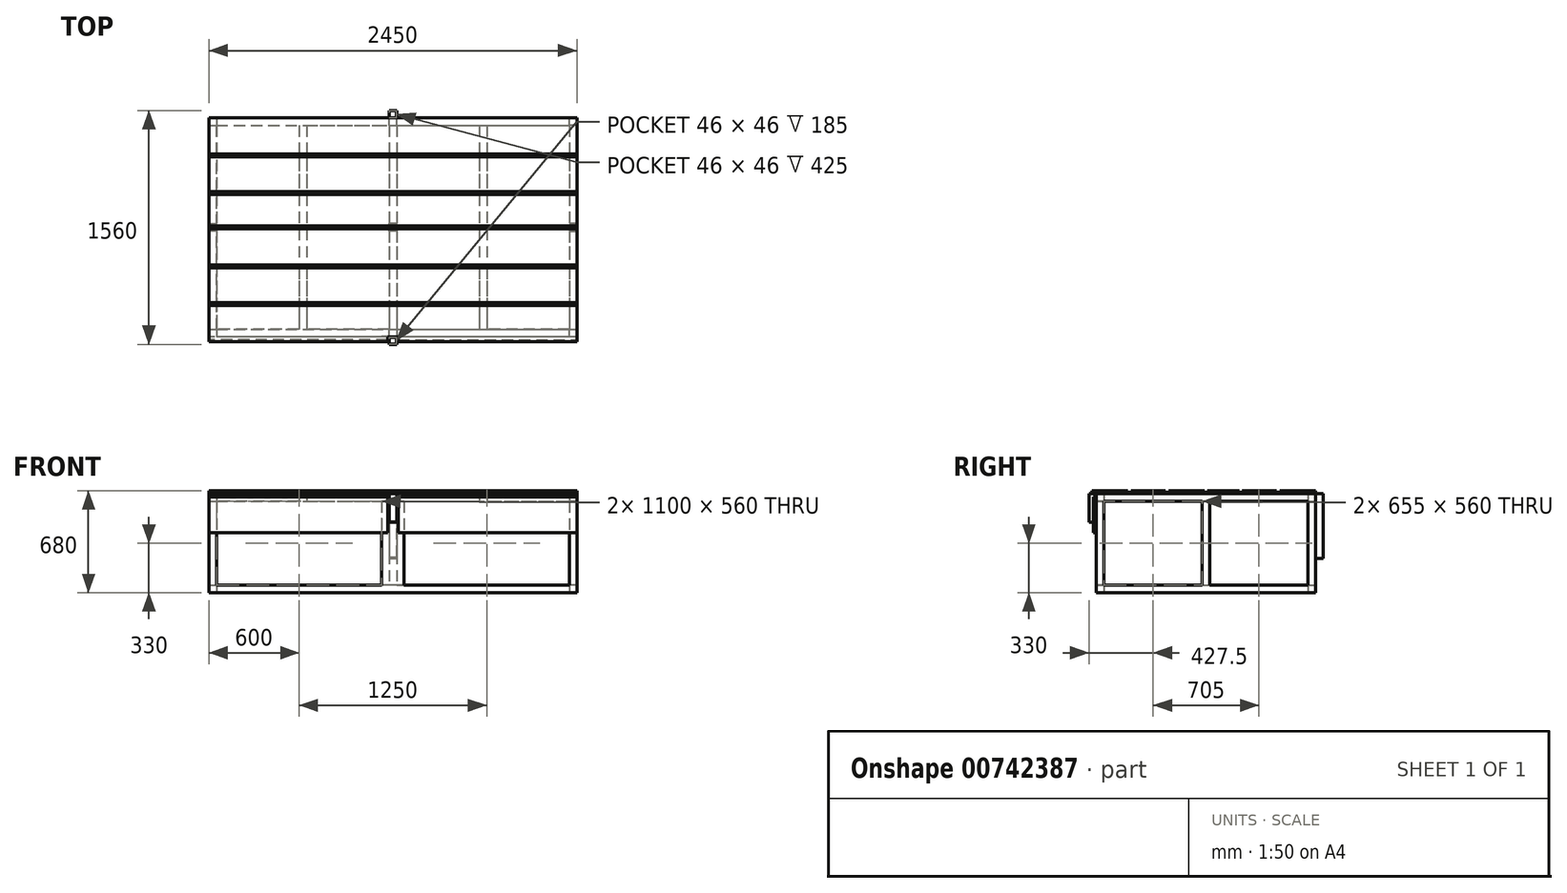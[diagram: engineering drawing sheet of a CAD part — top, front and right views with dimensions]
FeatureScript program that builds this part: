
annotation { "Feature Type Name" : "Feature", "Feature Type Description" : "" }
export const myFeature = defineFeature(function(context is Context, id is Id, definition is map)
    precondition{}
    {
        {
            var Q0;
            Q0=qCreatedBy(makeId("Top.planeOp"),FACE);
            var sketch = newSketch(context, id + "F0", { "sketchPlane" : qUnion([Q0])});
            skLineSegment(sketch, "E0.bottom", {"start": v(1225, -730) * mm, "end": v(-1225, -730) * mm});
            skLineSegment(sketch, "E0.top", {"start": v(1225, 730) * mm, "end": v(-1225, 730) * mm});
            skLineSegment(sketch, "E0.left", {"start": v(1225, -730) * mm, "end": v(1225, 730) * mm});
            skLineSegment(sketch, "E0.right", {"start": v(-1225, -730) * mm, "end": v(-1225, 730) * mm});
            skPoint(sketch, "E0.middle", {"position": v(0, 0) * mm});
            skLineSegment(sketch, "E1.bottom", {"start": v(-1175, 680) * mm, "end": v(1175, 680) * mm});
            skLineSegment(sketch, "E1.top", {"start": v(-1175, -680) * mm, "end": v(1175, -680) * mm});
            skLineSegment(sketch, "E1.left", {"start": v(-1175, 680) * mm, "end": v(-1175, -680) * mm});
            skLineSegment(sketch, "E1.right", {"start": v(1175, 680) * mm, "end": v(1175, -680) * mm});
            skLineSegment(sketch, "E2.bottom", {"start": v(25, 680) * mm, "end": v(-25, 680) * mm});
            skLineSegment(sketch, "E2.top", {"start": v(25, -680) * mm, "end": v(-25, -680) * mm});
            skLineSegment(sketch, "E2.left", {"start": v(25, 680) * mm, "end": v(25, -680) * mm});
            skLineSegment(sketch, "E2.right", {"start": v(-25, 680) * mm, "end": v(-25, -680) * mm});
            skSolve(sketch);
        }
        {
            var Q0;
            Q0=qSketchRegion(id+"F0",true);
            var Q1;
            Q1=makeQuery(id+"F0.imprint","IMPRINT",FACE,{"disambiguationData":[TD([[makeQuery(id+"F0.imprint","IMPRINT",EDGE,{"derivedFrom":sQuery(id+"F0.wireOp",EDGE,"E2.bottom")}),1.0]])]});
            extrude(context, id + "F1", {"entities" : qUnion([Q0, Q1]), "depth" : 50 * mm, "offsetDistance" : 25 * mm});
        }
        {
            var Q0;
            Q0=makeQuery(id+"F1.opExtrude","CAP_FACE",FACE,{"disambiguationData":[OSD([sQuery(id+"F0.wireOp",EDGE,"E0.bottom"),sQuery(id+"F0.wireOp",EDGE,"E0.top"),sQuery(id+"F0.wireOp",EDGE,"E0.left"),sQuery(id+"F0.wireOp",EDGE,"E0.right"),sQuery(id+"F0.wireOp",EDGE,"E1.bottom"),sQuery(id+"F0.wireOp",EDGE,"E1.top"),sQuery(id+"F0.wireOp",EDGE,"E1.left"),sQuery(id+"F0.wireOp",EDGE,"E1.right"),sQuery(id+"F0.wireOp",EDGE,"E2.left"),sQuery(id+"F0.wireOp",EDGE,"E2.right")])],"isStart":false});
            var sketch = newSketch(context, id + "F2", { "sketchPlane" : qUnion([Q0])});
            skLineSegment(sketch, "E3.bottom", {"start": v(-1225, 730) * mm, "end": v(-1175, 730) * mm});
            skLineSegment(sketch, "E3.top", {"start": v(-1225, 680) * mm, "end": v(-1175, 680) * mm});
            skLineSegment(sketch, "E3.left", {"start": v(-1225, 730) * mm, "end": v(-1225, 680) * mm});
            skLineSegment(sketch, "E3.right", {"start": v(-1175, 730) * mm, "end": v(-1175, 680) * mm});
            skLineSegment(sketch, "E4", {"start": v(-25, 680) * mm, "end": v(-25, 730) * mm});
            skLineSegment(sketch, "E5", {"start": v(25, 680) * mm, "end": v(25, 730) * mm});
            skLineSegment(sketch, "E6", {"start": v(25, 730) * mm, "end": v(-25, 730) * mm});
            skLineSegment(sketch, "E7", {"start": v(-25, 680) * mm, "end": v(25, 680) * mm});
            skLineSegment(sketch, "E8", {"start": v(1175, 680) * mm, "end": v(1175, 730) * mm});
            skLineSegment(sketch, "E9", {"start": v(1175, 730) * mm, "end": v(1225, 730) * mm});
            skLineSegment(sketch, "E10", {"start": v(1225, 730) * mm, "end": v(1225, 680) * mm});
            skLineSegment(sketch, "E11", {"start": v(1225, 680) * mm, "end": v(1175, 680) * mm});
            skLineSegment(sketch, "E12", {"start": v(1175, -680) * mm, "end": v(1225, -680) * mm});
            skLineSegment(sketch, "E13", {"start": v(1225, -680) * mm, "end": v(1225, -730) * mm});
            skLineSegment(sketch, "E14", {"start": v(1225, -730) * mm, "end": v(1175, -730) * mm});
            skLineSegment(sketch, "E15", {"start": v(1175, -730) * mm, "end": v(1175, -680) * mm});
            skLineSegment(sketch, "E16", {"start": v(-25, -680) * mm, "end": v(25, -680) * mm});
            skLineSegment(sketch, "E17", {"start": v(25, -680) * mm, "end": v(25, -730) * mm});
            skLineSegment(sketch, "E18", {"start": v(25, -730) * mm, "end": v(-25, -730) * mm});
            skLineSegment(sketch, "E19", {"start": v(-25, -730) * mm, "end": v(-25, -680) * mm});
            skLineSegment(sketch, "E20", {"start": v(-1175, -680) * mm, "end": v(-1175, -730) * mm});
            skLineSegment(sketch, "E21", {"start": v(-1175, -730) * mm, "end": v(-1225, -730) * mm});
            skLineSegment(sketch, "E22", {"start": v(-1225, -730) * mm, "end": v(-1225, -680) * mm});
            skLineSegment(sketch, "E23", {"start": v(-1225, -680) * mm, "end": v(-1175, -680) * mm});
            skLineSegment(sketch, "E24.bottom", {"start": v(25, -25) * mm, "end": v(-25, -25) * mm});
            skLineSegment(sketch, "E24.top", {"start": v(25, 25) * mm, "end": v(-25, 25) * mm});
            skLineSegment(sketch, "E24.left", {"start": v(25, -25) * mm, "end": v(25, 25) * mm});
            skLineSegment(sketch, "E24.right", {"start": v(-25, -25) * mm, "end": v(-25, 25) * mm});
            skPoint(sketch, "E24.middle", {"position": v(0, 0) * mm});
            skLineSegment(sketch, "E25", {"start": v(0, 0) * mm, "end": v(-1225, 0) * mm});
            skLineSegment(sketch, "E26", {"start": v(-1225, 25) * mm, "end": v(-1175, 25) * mm});
            skLineSegment(sketch, "E27", {"start": v(-1175, 25) * mm, "end": v(-1175, -25) * mm});
            skLineSegment(sketch, "E28", {"start": v(-1175, -25) * mm, "end": v(-1225, -25) * mm});
            skLineSegment(sketch, "E29", {"start": v(-1225, 25) * mm, "end": v(-1225, -25) * mm});
            skLineSegment(sketch, "E30.MirrorCS", {"start": v(1225, 25) * mm, "end": v(1225, -25) * mm});
            skLineSegment(sketch, "E31.MirrorCS", {"start": v(1175, -25) * mm, "end": v(1225, -25) * mm});
            skLineSegment(sketch, "E32.MirrorCS", {"start": v(1225, 25) * mm, "end": v(1175, 25) * mm});
            skLineSegment(sketch, "E33.MirrorCS", {"start": v(1175, 25) * mm, "end": v(1175, -25) * mm});
            skSolve(sketch);
        }
        {
            var Q0;
            Q0=qSketchRegion(id+"F2",true);
            extrude(context, id + "F3", {"entities" : qUnion([Q0]), "operationType" : NewBodyOperationType.ADD, "depth" : 560 * mm, "offsetDistance" : 25 * mm});
        }
        {
            var Q0;
            Q0=makeQuery(id+"F3.opExtrude","CAP_FACE",FACE,{"disambiguationData":[OSD([sQuery(id+"F2.wireOp",EDGE,"E26"),sQuery(id+"F2.wireOp",EDGE,"E27"),sQuery(id+"F2.wireOp",EDGE,"E28"),sQuery(id+"F2.wireOp",EDGE,"E29")])],"isStart":false});
            var sketch = newSketch(context, id + "F4", { "sketchPlane" : qUnion([Q0])});
            skLineSegment(sketch, "E34", {"start": v(-1225, 25) * mm, "end": v(-1225, 730) * mm});
            skLineSegment(sketch, "E35", {"start": v(-1225, 730) * mm, "end": v(-1175, 730) * mm});
            skLineSegment(sketch, "E36", {"start": v(-1175, 730) * mm, "end": v(1225, 730) * mm});
            skLineSegment(sketch, "E37", {"start": v(1225, 730) * mm, "end": v(1225, -730) * mm});
            skLineSegment(sketch, "E38", {"start": v(1225, -730) * mm, "end": v(-1225, -730) * mm});
            skLineSegment(sketch, "E39", {"start": v(-1225, -730) * mm, "end": v(-1225, 25) * mm});
            skLineSegment(sketch, "E40", {"start": v(-1175, 730) * mm, "end": v(-1175, 680) * mm});
            skLineSegment(sketch, "E41", {"start": v(-1175, 680) * mm, "end": v(-25, 680) * mm});
            skLineSegment(sketch, "E42", {"start": v(-1175, 680) * mm, "end": v(-600, 680) * mm});
            skLineSegment(sketch, "E43", {"start": v(-600, 680) * mm, "end": v(-575, 680) * mm});
            skLineSegment(sketch, "E44", {"start": v(-600, 680) * mm, "end": v(-625, 680) * mm});
            skLineSegment(sketch, "E45", {"start": v(-625, 680) * mm, "end": v(-625, -680) * mm});
            skLineSegment(sketch, "E46.MirrorCS", {"start": v(-575, 680) * mm, "end": v(-575, -680) * mm});
            skLineSegment(sketch, "E47", {"start": v(-25, 680) * mm, "end": v(25, 680) * mm});
            skLineSegment(sketch, "E48", {"start": v(25, 680) * mm, "end": v(1175, 680) * mm});
            skLineSegment(sketch, "E49", {"start": v(25, 680) * mm, "end": v(600, 680) * mm});
            skLineSegment(sketch, "E50", {"start": v(600, 680) * mm, "end": v(575, 680) * mm});
            skLineSegment(sketch, "E51", {"start": v(575, 680) * mm, "end": v(575, -680) * mm});
            skLineSegment(sketch, "E52.MirrorCS", {"start": v(625, 680) * mm, "end": v(625, -680) * mm});
            skLineSegment(sketch, "E53", {"start": v(-25, 680) * mm, "end": v(-25, -680) * mm});
            skLineSegment(sketch, "E54", {"start": v(-25, -680) * mm, "end": v(-575, -680) * mm});
            skLineSegment(sketch, "E55", {"start": v(-625, -680) * mm, "end": v(-1175, -680) * mm});
            skLineSegment(sketch, "E56", {"start": v(-1175, -680) * mm, "end": v(-1175, 680) * mm});
            skLineSegment(sketch, "E57", {"start": v(1175, 680) * mm, "end": v(1175, -680) * mm});
            skLineSegment(sketch, "E58", {"start": v(1175, -680) * mm, "end": v(625, -680) * mm});
            skLineSegment(sketch, "E59", {"start": v(25, 680) * mm, "end": v(25, -680) * mm});
            skLineSegment(sketch, "E60", {"start": v(25, -680) * mm, "end": v(575, -680) * mm});
            skSolve(sketch);
        }
        {
            var Q0;
            Q0=qSketchRegion(id+"F4",true);
            extrude(context, id + "F5", {"entities" : qUnion([Q0]), "operationType" : NewBodyOperationType.ADD, "depth" : 50 * mm, "offsetDistance" : 25 * mm});
        }
        {
            var Q0;
            {var subQ5=sQuery(id+"F0.wireOp",EDGE,"E1.left");var subQ6=sQuery(id+"F0.wireOp",EDGE,"E1.top");var subQ8=makeQuery(id+"F1.opExtrude","CAP_EDGE",EDGE,{"disambiguationData":[OSD([subQ6]),TDD([makeQuery(id+"F0.imprint","IMPRINT",EDGE,{"disambiguationData":[TD([[makeQuery(id+"F0.imprint","INTERSECT",VERTEX,{"derivedFrom":[subQ6,subQ5]}),-1.0]])],"derivedFrom":subQ6})])],"isStart":false});Q0=makeQuery(id+"F2.imprint","IMPRINT",FACE,{"disambiguationData":[TD([[makeQuery(id+"F2.imprint","IMPRINT",EDGE,{"derivedFrom":subQ8}),1.0]])]});}
            cPlane(context, id + "F6", {"entities" : qUnion([Q0]), "cplaneType" : CPlaneType.OFFSET, "offset" : 420 * mm, "width" : 150 * mm, "height" : 150 * mm});
        }
        {
            var Q0;
            Q0=qCreatedBy(id+"F6.planeOp",FACE);
            var sketch = newSketch(context, id + "F7", { "sketchPlane" : qUnion([Q0])});
            skLineSegment(sketch, "E61.bottom", {"start": v(-25, -730) * mm, "end": v(25, -730) * mm});
            skLineSegment(sketch, "E61.top", {"start": v(-25, -780) * mm, "end": v(25, -780) * mm});
            skLineSegment(sketch, "E61.left", {"start": v(-25, -730) * mm, "end": v(-25, -780) * mm});
            skLineSegment(sketch, "E61.right", {"start": v(25, -730) * mm, "end": v(25, -780) * mm});
            skSolve(sketch);
        }
        {
            var Q0;
            Q0 = qSketchRegion(id + "F7", true);
            extrude(context, id + "F8", {"entities" : qUnion([Q0]), "operationType" : NewBodyOperationType.ADD, "depth" : 5 * mm, "offsetDistance" : 25 * mm});
        }
        {
            var Q0;
            Q0=makeQuery(id+"F8.opExtrude","CAP_FACE",FACE,{"disambiguationData":[OSD([sQuery(id+"F7.wireOp",EDGE,"E61.bottom"),sQuery(id+"F7.wireOp",EDGE,"E61.top"),sQuery(id+"F7.wireOp",EDGE,"E61.left"),sQuery(id+"F7.wireOp",EDGE,"E61.right")])],"isStart":false});
            var sketch = newSketch(context, id + "F9", { "sketchPlane" : qUnion([Q0])});
            skLineSegment(sketch, "E62.bottom", {"start": v(-25, -730) * mm, "end": v(25, -730) * mm});
            skLineSegment(sketch, "E62.top", {"start": v(-25, -780) * mm, "end": v(25, -780) * mm});
            skLineSegment(sketch, "E62.left", {"start": v(-25, -730) * mm, "end": v(-25, -780) * mm});
            skLineSegment(sketch, "E62.right", {"start": v(25, -730) * mm, "end": v(25, -780) * mm});
            skLineSegment(sketch, "E63.bottom", {"start": v(25, -780) * mm, "end": v(23, -780) * mm});
            skLineSegment(sketch, "E63.top", {"start": v(25, -778) * mm, "end": v(23, -778) * mm});
            skLineSegment(sketch, "E63.left", {"start": v(25, -780) * mm, "end": v(25, -778) * mm});
            skLineSegment(sketch, "E63.right", {"start": v(23, -780) * mm, "end": v(23, -778) * mm});
            skLineSegment(sketch, "E64.bottom", {"start": v(23, -778) * mm, "end": v(-23, -778) * mm});
            skLineSegment(sketch, "E64.top", {"start": v(23, -732) * mm, "end": v(-23, -732) * mm});
            skLineSegment(sketch, "E64.left", {"start": v(23, -778) * mm, "end": v(23, -732) * mm});
            skLineSegment(sketch, "E64.right", {"start": v(-23, -778) * mm, "end": v(-23, -732) * mm});
            skSolve(sketch);
        }
        {
            var Q0;
            Q0 = qSketchRegion(id + "F9", true);
            var Q1;
            {var subQ0=sQuery(id+"F4.wireOp",EDGE,"E60");var subQ1=sQuery(id+"F4.wireOp",EDGE,"E59");var subQ2=sQuery(id+"F4.wireOp",EDGE,"E58");var subQ3=sQuery(id+"F4.wireOp",EDGE,"E57");var subQ4=sQuery(id+"F4.wireOp",EDGE,"E56");var subQ5=sQuery(id+"F4.wireOp",EDGE,"E55");var subQ6=sQuery(id+"F4.wireOp",EDGE,"E54");var subQ7=sQuery(id+"F4.wireOp",EDGE,"E53");var subQ8=sQuery(id+"F4.wireOp",EDGE,"E52.MirrorCS");var subQ9=sQuery(id+"F4.wireOp",EDGE,"E51");var subQ10=sQuery(id+"F4.wireOp",EDGE,"E49");var subQ11=sQuery(id+"F4.wireOp",EDGE,"E48");var subQ12=sQuery(id+"F4.wireOp",EDGE,"E46.MirrorCS");var subQ13=sQuery(id+"F4.wireOp",EDGE,"E45");var subQ14=sQuery(id+"F4.wireOp",EDGE,"E42");var subQ15=sQuery(id+"F4.wireOp",EDGE,"E41");var subQ16=sQuery(id+"F4.wireOp",EDGE,"E39");var subQ17=sQuery(id+"F4.wireOp",EDGE,"E38");var subQ18=sQuery(id+"F4.wireOp",EDGE,"E37");var subQ19=sQuery(id+"F4.wireOp",EDGE,"E36");var subQ20=sQuery(id+"F4.wireOp",EDGE,"E35");var subQ21=sQuery(id+"F4.wireOp",EDGE,"E34");Q1=makeQuery(id+"FP4IzDu3Lu8PIDH_1.boolean.opBoolean","MERGE",FACE,{"derivedFrom":[makeQuery(id+"F5.opExtrude","CAP_FACE",FACE,{"disambiguationData":[OSD([subQ21,subQ20,subQ19,subQ18,subQ17,subQ16,subQ15,subQ14,subQ13,subQ12,subQ11,subQ10,subQ9,subQ8,subQ7,subQ6,subQ5,subQ4,subQ3,subQ2,subQ1,subQ0])],"isStart":false}),makeQuery(id+"FP4IzDu3Lu8PIDH_1.opExtrude","CAP_FACE",FACE,{"disambiguationData":[OSD([subQ21,subQ20,subQ19,subQ18,subQ17,subQ16,subQ15,subQ14,subQ13,subQ12,subQ11,subQ10,subQ9,subQ8,subQ7,subQ6,subQ5,subQ4,subQ3,subQ2,subQ1,subQ0])],"isStart":false})]});}
            extrude(context, id + "F10", {"entities" : qUnion([Q0]), "operationType" : NewBodyOperationType.ADD, "endBound" : BoundingType.UP_TO_SURFACE, "depth" : 25 * mm, "endBoundEntityFace" : qUnion([Q1]), "offsetDistance" : 25 * mm});
        }
        {
            var Q0;
            {var subQ5=sQuery(id+"F0.wireOp",EDGE,"E1.left");var subQ6=sQuery(id+"F0.wireOp",EDGE,"E1.top");var subQ8=makeQuery(id+"F1.opExtrude","CAP_EDGE",EDGE,{"disambiguationData":[OSD([subQ6]),TDD([makeQuery(id+"F0.imprint","IMPRINT",EDGE,{"disambiguationData":[TD([[makeQuery(id+"F0.imprint","INTERSECT",VERTEX,{"derivedFrom":[subQ6,subQ5]}),-1.0]])],"derivedFrom":subQ6})])],"isStart":false});Q0=makeQuery(id+"F2.imprint","IMPRINT",FACE,{"disambiguationData":[TD([[makeQuery(id+"F2.imprint","IMPRINT",EDGE,{"derivedFrom":subQ8}),1.0]])]});}
            cPlane(context, id + "F11", {"entities" : qUnion([Q0]), "cplaneType" : CPlaneType.OFFSET, "offset" : 180 * mm, "width" : 150 * mm, "height" : 150 * mm});
        }
        {
            var Q0;
            Q0=qCreatedBy(id+"F11.planeOp",FACE);
            var sketch = newSketch(context, id + "F12", { "sketchPlane" : qUnion([Q0])});
            skLineSegment(sketch, "E65.bottom", {"start": v(-25, 730) * mm, "end": v(25, 730) * mm});
            skLineSegment(sketch, "E65.top", {"start": v(-25, 780) * mm, "end": v(25, 780) * mm});
            skLineSegment(sketch, "E65.left", {"start": v(-25, 730) * mm, "end": v(-25, 780) * mm});
            skLineSegment(sketch, "E65.right", {"start": v(25, 730) * mm, "end": v(25, 780) * mm});
            skSolve(sketch);
        }
        {
            var Q0;
            Q0=makeQuery(id+"F12.imprint","IMPRINT",FACE,{"disambiguationData":[TD([[makeQuery(id+"F12.imprint","IMPRINT",EDGE,{"derivedFrom":sQuery(id+"F12.wireOp",EDGE,"E65.bottom")}),1.0]])]});
            extrude(context, id + "F13", {"entities" : qUnion([Q0]), "operationType" : NewBodyOperationType.ADD, "depth" : 5 * mm, "offsetDistance" : 25 * mm});
        }
        {
            var Q0;
            Q0=makeQuery(id+"F3.opExtrude","SWEPT_FACE",FACE,{"disambiguationData":[OSD([sQuery(id+"F2.wireOp",EDGE,"E17")])]});
            cPlane(context, id + "F14", {"entities" : qUnion([Q0]), "cplaneType" : CPlaneType.OFFSET, "offset" : 25 * mm, "oppositeDirection" : true, "width" : 150 * mm, "height" : 150 * mm});
        }
        {
            var Q0;
            Q0=qCreatedBy(id+"F14.planeOp",FACE);
            var sketch = newSketch(context, id + "F15", { "sketchPlane" : qUnion([Q0])});
            skLineSegment(sketch, "E66.bottom", {"start": v(-730, 610) * mm, "end": v(-725, 610) * mm});
            skLineSegment(sketch, "E66.top", {"start": v(-730, 50) * mm, "end": v(-725, 50) * mm});
            skLineSegment(sketch, "E66.left", {"start": v(-730, 610) * mm, "end": v(-730, 50) * mm});
            skLineSegment(sketch, "E66.right", {"start": v(-725, 610) * mm, "end": v(-725, 50) * mm});
            skLineSegment(sketch, "E67.bottom", {"start": v(730, 610) * mm, "end": v(725, 610) * mm});
            skLineSegment(sketch, "E67.top", {"start": v(730, 50) * mm, "end": v(725, 50) * mm});
            skLineSegment(sketch, "E67.left", {"start": v(730, 610) * mm, "end": v(730, 50) * mm});
            skLineSegment(sketch, "E67.right", {"start": v(725, 610) * mm, "end": v(725, 50) * mm});
            skSolve(sketch);
        }
        {
            var Q0;
            Q0 = qSketchRegion(id + "F15", true);
            extrude(context, id + "F16", {"entities" : qUnion([Q0]), "operationType" : NewBodyOperationType.ADD, "depth" : 75 * mm, "offsetDistance" : 25 * mm, "hasSecondDirection" : true, "secondDirectionOppositeDirection" : true, "secondDirectionDepth" : 75 * mm});
        }
        {
            var Q0;
            Q0=makeQuery(id+"F13.opExtrude","CAP_FACE",FACE,{"disambiguationData":[OSD([sQuery(id+"F12.wireOp",EDGE,"E65.bottom"),sQuery(id+"F12.wireOp",EDGE,"E65.top"),sQuery(id+"F12.wireOp",EDGE,"E65.left"),sQuery(id+"F12.wireOp",EDGE,"E65.right")])],"isStart":false});
            var sketch = newSketch(context, id + "F17", { "sketchPlane" : qUnion([Q0])});
            skLineSegment(sketch, "E68.bottom", {"start": v(-25, 780) * mm, "end": v(25, 780) * mm});
            skLineSegment(sketch, "E68.top", {"start": v(-25, 730) * mm, "end": v(25, 730) * mm});
            skLineSegment(sketch, "E68.left", {"start": v(-25, 780) * mm, "end": v(-25, 730) * mm});
            skLineSegment(sketch, "E68.right", {"start": v(25, 780) * mm, "end": v(25, 730) * mm});
            skLineSegment(sketch, "E69.bottom", {"start": v(25, 730) * mm, "end": v(23, 730) * mm});
            skLineSegment(sketch, "E69.top", {"start": v(25, 732) * mm, "end": v(23, 732) * mm});
            skLineSegment(sketch, "E69.left", {"start": v(25, 730) * mm, "end": v(25, 732) * mm});
            skLineSegment(sketch, "E70.bottom", {"start": v(23, 732) * mm, "end": v(-23, 732) * mm});
            skLineSegment(sketch, "E70.top", {"start": v(23, 778) * mm, "end": v(-23, 778) * mm});
            skLineSegment(sketch, "E70.left", {"start": v(23, 732) * mm, "end": v(23, 778) * mm});
            skLineSegment(sketch, "E70.right", {"start": v(-23, 732) * mm, "end": v(-23, 778) * mm});
            skSolve(sketch);
        }
        {
            var Q0;
            Q0 = qSketchRegion(id + "F17", true);
            var Q1;
            {var subQ0=sQuery(id+"F4.wireOp",EDGE,"E60");var subQ1=sQuery(id+"F4.wireOp",EDGE,"E59");var subQ2=sQuery(id+"F4.wireOp",EDGE,"E58");var subQ3=sQuery(id+"F4.wireOp",EDGE,"E57");var subQ4=sQuery(id+"F4.wireOp",EDGE,"E56");var subQ5=sQuery(id+"F4.wireOp",EDGE,"E55");var subQ6=sQuery(id+"F4.wireOp",EDGE,"E54");var subQ7=sQuery(id+"F4.wireOp",EDGE,"E53");var subQ8=sQuery(id+"F4.wireOp",EDGE,"E52.MirrorCS");var subQ9=sQuery(id+"F4.wireOp",EDGE,"E51");var subQ10=sQuery(id+"F4.wireOp",EDGE,"E49");var subQ11=sQuery(id+"F4.wireOp",EDGE,"E48");var subQ12=sQuery(id+"F4.wireOp",EDGE,"E46.MirrorCS");var subQ13=sQuery(id+"F4.wireOp",EDGE,"E45");var subQ14=sQuery(id+"F4.wireOp",EDGE,"E42");var subQ15=sQuery(id+"F4.wireOp",EDGE,"E41");var subQ16=sQuery(id+"F4.wireOp",EDGE,"E39");var subQ17=sQuery(id+"F4.wireOp",EDGE,"E38");var subQ18=sQuery(id+"F4.wireOp",EDGE,"E37");var subQ19=sQuery(id+"F4.wireOp",EDGE,"E36");var subQ20=sQuery(id+"F4.wireOp",EDGE,"E35");var subQ21=sQuery(id+"F4.wireOp",EDGE,"E34");Q1=makeQuery(id+"F10.boolean.opBoolean","MERGE",FACE,{"derivedFrom":[makeQuery(id+"F5.opExtrude","CAP_FACE",FACE,{"disambiguationData":[OSD([subQ21,subQ20,subQ19,subQ18,subQ17,subQ16,subQ15,subQ14,subQ13,subQ12,subQ11,subQ10,subQ9,subQ8,subQ7,subQ6,subQ5,subQ4,subQ3,subQ2,subQ1,subQ0])],"isStart":false}),makeQuery(id+"F10.opExtrude","CAP_FACE",FACE,{"disambiguationData":[OSD([subQ21,subQ20,subQ19,subQ18,subQ17,subQ16,subQ15,subQ14,subQ13,subQ12,subQ11,subQ10,subQ9,subQ8,subQ7,subQ6,subQ5,subQ4,subQ3,subQ2,subQ1,subQ0])],"isStart":false})]});}
            extrude(context, id + "F18", {"entities" : qUnion([Q0]), "operationType" : NewBodyOperationType.ADD, "endBound" : BoundingType.UP_TO_SURFACE, "depth" : 25 * mm, "endBoundEntityFace" : qUnion([Q1]), "offsetDistance" : 25 * mm});
        }
        {
            var Q0;
            {var subQ0=sQuery(id+"F4.wireOp",EDGE,"E60");var subQ1=sQuery(id+"F4.wireOp",EDGE,"E59");var subQ2=sQuery(id+"F4.wireOp",EDGE,"E58");var subQ3=sQuery(id+"F4.wireOp",EDGE,"E57");var subQ4=sQuery(id+"F4.wireOp",EDGE,"E56");var subQ5=sQuery(id+"F4.wireOp",EDGE,"E55");var subQ6=sQuery(id+"F4.wireOp",EDGE,"E54");var subQ7=sQuery(id+"F4.wireOp",EDGE,"E53");var subQ8=sQuery(id+"F4.wireOp",EDGE,"E52.MirrorCS");var subQ9=sQuery(id+"F4.wireOp",EDGE,"E51");var subQ10=sQuery(id+"F4.wireOp",EDGE,"E49");var subQ11=sQuery(id+"F4.wireOp",EDGE,"E48");var subQ12=sQuery(id+"F4.wireOp",EDGE,"E46.MirrorCS");var subQ13=sQuery(id+"F4.wireOp",EDGE,"E45");var subQ14=sQuery(id+"F4.wireOp",EDGE,"E42");var subQ15=sQuery(id+"F4.wireOp",EDGE,"E41");var subQ16=sQuery(id+"F4.wireOp",EDGE,"E39");var subQ17=sQuery(id+"F4.wireOp",EDGE,"E38");var subQ18=sQuery(id+"F4.wireOp",EDGE,"E37");var subQ19=sQuery(id+"F4.wireOp",EDGE,"E36");var subQ20=sQuery(id+"F4.wireOp",EDGE,"E35");var subQ21=sQuery(id+"F4.wireOp",EDGE,"E34");Q0=makeQuery(id+"F18.boolean.opBoolean","MERGE",FACE,{"derivedFrom":[makeQuery(id+"F10.boolean.opBoolean","MERGE",FACE,{"derivedFrom":[makeQuery(id+"F5.opExtrude","CAP_FACE",FACE,{"disambiguationData":[OSD([subQ21,subQ20,subQ19,subQ18,subQ17,subQ16,subQ15,subQ14,subQ13,subQ12,subQ11,subQ10,subQ9,subQ8,subQ7,subQ6,subQ5,subQ4,subQ3,subQ2,subQ1,subQ0])],"isStart":false}),makeQuery(id+"F10.opExtrude","CAP_FACE",FACE,{"disambiguationData":[OSD([subQ21,subQ20,subQ19,subQ18,subQ17,subQ16,subQ15,subQ14,subQ13,subQ12,subQ11,subQ10,subQ9,subQ8,subQ7,subQ6,subQ5,subQ4,subQ3,subQ2,subQ1,subQ0])],"isStart":false})]}),makeQuery(id+"F18.opExtrude","CAP_FACE",FACE,{"disambiguationData":[OSD([subQ21,subQ20,subQ19,subQ18,subQ17,subQ16,subQ15,subQ14,subQ13,subQ12,subQ11,subQ10,subQ9,subQ8,subQ7,subQ6,subQ5,subQ4,subQ3,subQ2,subQ1,subQ0])],"isStart":false})]});}
            var sketch = newSketch(context, id + "F19", { "sketchPlane" : qUnion([Q0])});
            skLineSegment(sketch, "E71.bottom", {"start": v(-1225, 730) * mm, "end": v(1225, 730) * mm});
            skLineSegment(sketch, "E71.top", {"start": v(-1225, -730) * mm, "end": v(1225, -730) * mm});
            skLineSegment(sketch, "E71.left", {"start": v(-1225, 730) * mm, "end": v(-1225, -730) * mm});
            skLineSegment(sketch, "E71.right", {"start": v(1225, 730) * mm, "end": v(1225, -730) * mm});
            skLineSegment(sketch, "E72", {"start": v(1225, -730) * mm, "end": v(1225, -760) * mm});
            skLineSegment(sketch, "E73.top", {"start": v(1225, -730) * mm, "end": v(46.2, -730) * mm});
            skLineSegment(sketch, "E73.left", {"start": v(1225, -760) * mm, "end": v(1225, -730) * mm});
            skLineSegment(sketch, "E74.top", {"start": v(46.2, -730) * mm, "end": v(-45, -730) * mm});
            skLineSegment(sketch, "E75.top", {"start": v(-45, -730) * mm, "end": v(-1225, -730) * mm});
            skLineSegment(sketch, "E75.right", {"start": v(-1225, -760) * mm, "end": v(-1225, -730) * mm});
            skLineSegment(sketch, "E76", {"start": v(35, -760) * mm, "end": v(35, -730) * mm});
            skLineSegment(sketch, "E77", {"start": v(-35, -760) * mm, "end": v(-35, -730) * mm});
            skLineSegment(sketch, "E78", {"start": v(35, -760) * mm, "end": v(1225, -760) * mm});
            skLineSegment(sketch, "E79", {"start": v(-1225, -760) * mm, "end": v(-35, -760) * mm});
            skSolve(sketch);
        }
        {
            var Q0;
            Q0 = qSketchRegion(id + "F19", true);
            extrude(context, id + "F20", {"entities" : qUnion([Q0]), "depth" : 20 * mm, "offsetDistance" : 25 * mm});
        }
        {
            var Q0;
            Q0=makeQuery(id+"F16.boolean.opBoolean","MERGE",FACE,{"derivedFrom":[makeQuery(id+"F5.boolean.opBoolean","MERGE",FACE,{"derivedFrom":[makeQuery(id+"F3.boolean.opBoolean","MERGE",FACE,{"derivedFrom":[makeQuery(id+"F1.opExtrude","SWEPT_FACE",FACE,{"disambiguationData":[OSD([sQuery(id+"F0.wireOp",EDGE,"E0.bottom")])]}),makeQuery(id+"F3.opExtrude","SWEPT_FACE",FACE,{"disambiguationData":[OSD([sQuery(id+"F2.wireOp",EDGE,"E14")])]}),makeQuery(id+"F3.opExtrude","SWEPT_FACE",FACE,{"disambiguationData":[OSD([sQuery(id+"F2.wireOp",EDGE,"E18")])]}),makeQuery(id+"F3.opExtrude","SWEPT_FACE",FACE,{"disambiguationData":[OSD([sQuery(id+"F2.wireOp",EDGE,"E21")])]})]}),makeQuery(id+"F5.opExtrude","SWEPT_FACE",FACE,{"disambiguationData":[OSD([sQuery(id+"F4.wireOp",EDGE,"E38")])]})]}),makeQuery(id+"F16.opExtrude","SWEPT_FACE",FACE,{"disambiguationData":[OSD([sQuery(id+"F15.wireOp",EDGE,"E66.left")])]})]});
            var sketch = newSketch(context, id + "F21", { "sketchPlane" : qUnion([Q0])});
            skLineSegment(sketch, "E80", {"start": v(-25, 660) * mm, "end": v(-35, 660) * mm});
            skLineSegment(sketch, "E81", {"start": v(-35, 660) * mm, "end": v(-35, 640) * mm});
            skLineSegment(sketch, "E82", {"start": v(25, 660) * mm, "end": v(35, 660) * mm});
            skLineSegment(sketch, "E83", {"start": v(35, 660) * mm, "end": v(35, 640) * mm});
            skLineSegment(sketch, "E84.bottom", {"start": v(-35, 640) * mm, "end": v(-1225, 640) * mm});
            skLineSegment(sketch, "E84.top", {"start": v(-35, 400) * mm, "end": v(-1225, 400) * mm});
            skLineSegment(sketch, "E84.left", {"start": v(-35, 640) * mm, "end": v(-35, 400) * mm});
            skLineSegment(sketch, "E84.right", {"start": v(-1225, 640) * mm, "end": v(-1225, 400) * mm});
            skLineSegment(sketch, "E85.bottom", {"start": v(35, 640) * mm, "end": v(1225, 640) * mm});
            skLineSegment(sketch, "E85.top", {"start": v(35, 400) * mm, "end": v(1225, 400) * mm});
            skLineSegment(sketch, "E85.left", {"start": v(35, 640) * mm, "end": v(35, 400) * mm});
            skLineSegment(sketch, "E85.right", {"start": v(1225, 640) * mm, "end": v(1225, 400) * mm});
            skSolve(sketch);
        }
        {
            var Q0;
            Q0 = qSketchRegion(id + "F21", true);
            extrude(context, id + "F22", {"entities" : qUnion([Q0]), "depth" : 20 * mm, "offsetDistance" : 25 * mm});
        }
        {
            var Q0;
            Q0=makeQuery(id+"F20.opExtrude","SWEPT_FACE",FACE,{"disambiguationData":[OSD([sQuery(id+"F19.wireOp",EDGE,"E71.left"),sQuery(id+"F19.wireOp",EDGE,"E75.right")])]});
            var sketch = newSketch(context, id + "F23", { "sketchPlane" : qUnion([Q0])});
            skLineSegment(sketch, "E86", {"start": v(730, 680) * mm, "end": v(10, 680) * mm});
            skLineSegment(sketch, "E87.bottom", {"start": v(10, 680) * mm, "end": v(-10, 680) * mm});
            skLineSegment(sketch, "E87.top", {"start": v(10, 660) * mm, "end": v(-10, 660) * mm});
            skLineSegment(sketch, "E87.left", {"start": v(10, 680) * mm, "end": v(10, 660) * mm});
            skLineSegment(sketch, "E87.right", {"start": v(-10, 680) * mm, "end": v(-10, 660) * mm});
            skLineSegment(sketch, "E88", {"start": v(-10, 680) * mm, "end": v(-133.71, 680) * mm});
            skLineSegment(sketch, "E89", {"start": v(730, 680) * mm, "end": v(520, 680) * mm});
            skLineSegment(sketch, "E90.bottom", {"start": v(520, 680) * mm, "end": v(500, 680) * mm});
            skLineSegment(sketch, "E90.top", {"start": v(520, 660) * mm, "end": v(500, 660) * mm});
            skLineSegment(sketch, "E90.left", {"start": v(520, 680) * mm, "end": v(520, 660) * mm});
            skLineSegment(sketch, "E90.right", {"start": v(500, 680) * mm, "end": v(500, 660) * mm});
            skLineSegment(sketch, "E91", {"start": v(500, 680) * mm, "end": v(270, 680) * mm});
            skLineSegment(sketch, "E92.bottom", {"start": v(270, 680) * mm, "end": v(250, 680) * mm});
            skLineSegment(sketch, "E92.top", {"start": v(270, 660) * mm, "end": v(250, 660) * mm});
            skLineSegment(sketch, "E92.left", {"start": v(270, 680) * mm, "end": v(270, 660) * mm});
            skLineSegment(sketch, "E92.right", {"start": v(250, 680) * mm, "end": v(250, 660) * mm});
            skLineSegment(sketch, "E93", {"start": v(-10, 680) * mm, "end": v(-220, 680) * mm});
            skLineSegment(sketch, "E94.bottom", {"start": v(-220, 680) * mm, "end": v(-240, 680) * mm});
            skLineSegment(sketch, "E94.top", {"start": v(-220, 660) * mm, "end": v(-240, 660) * mm});
            skLineSegment(sketch, "E94.left", {"start": v(-220, 680) * mm, "end": v(-220, 660) * mm});
            skLineSegment(sketch, "E94.right", {"start": v(-240, 680) * mm, "end": v(-240, 660) * mm});
            skLineSegment(sketch, "E95", {"start": v(-240, 680) * mm, "end": v(-470, 680) * mm});
            skLineSegment(sketch, "E96.bottom", {"start": v(-470, 680) * mm, "end": v(-490, 680) * mm});
            skLineSegment(sketch, "E96.top", {"start": v(-470, 660) * mm, "end": v(-490, 660) * mm});
            skLineSegment(sketch, "E96.left", {"start": v(-470, 680) * mm, "end": v(-470, 660) * mm});
            skLineSegment(sketch, "E96.right", {"start": v(-490, 680) * mm, "end": v(-490, 660) * mm});
            skLineSegment(sketch, "E97", {"start": v(730, 680) * mm, "end": v(730, 660) * mm});
            skSolve(sketch);
        }
        {
            var Q0;
            Q0 = qSketchRegion(id + "F23", true);
            var Q1;
            Q1=makeQuery(id+"F20.opExtrude","SWEPT_FACE",FACE,{"disambiguationData":[OSD([sQuery(id+"F19.wireOp",EDGE,"E71.right"),sQuery(id+"F19.wireOp",EDGE,"E73.left")])]});
            extrude(context, id + "F24", {"entities" : qUnion([Q0]), "operationType" : NewBodyOperationType.REMOVE, "endBound" : BoundingType.UP_TO_SURFACE, "oppositeDirection" : true, "depth" : 25 * mm, "endBoundEntityFace" : qUnion([Q1]), "offsetDistance" : 25 * mm});
        }
    });
